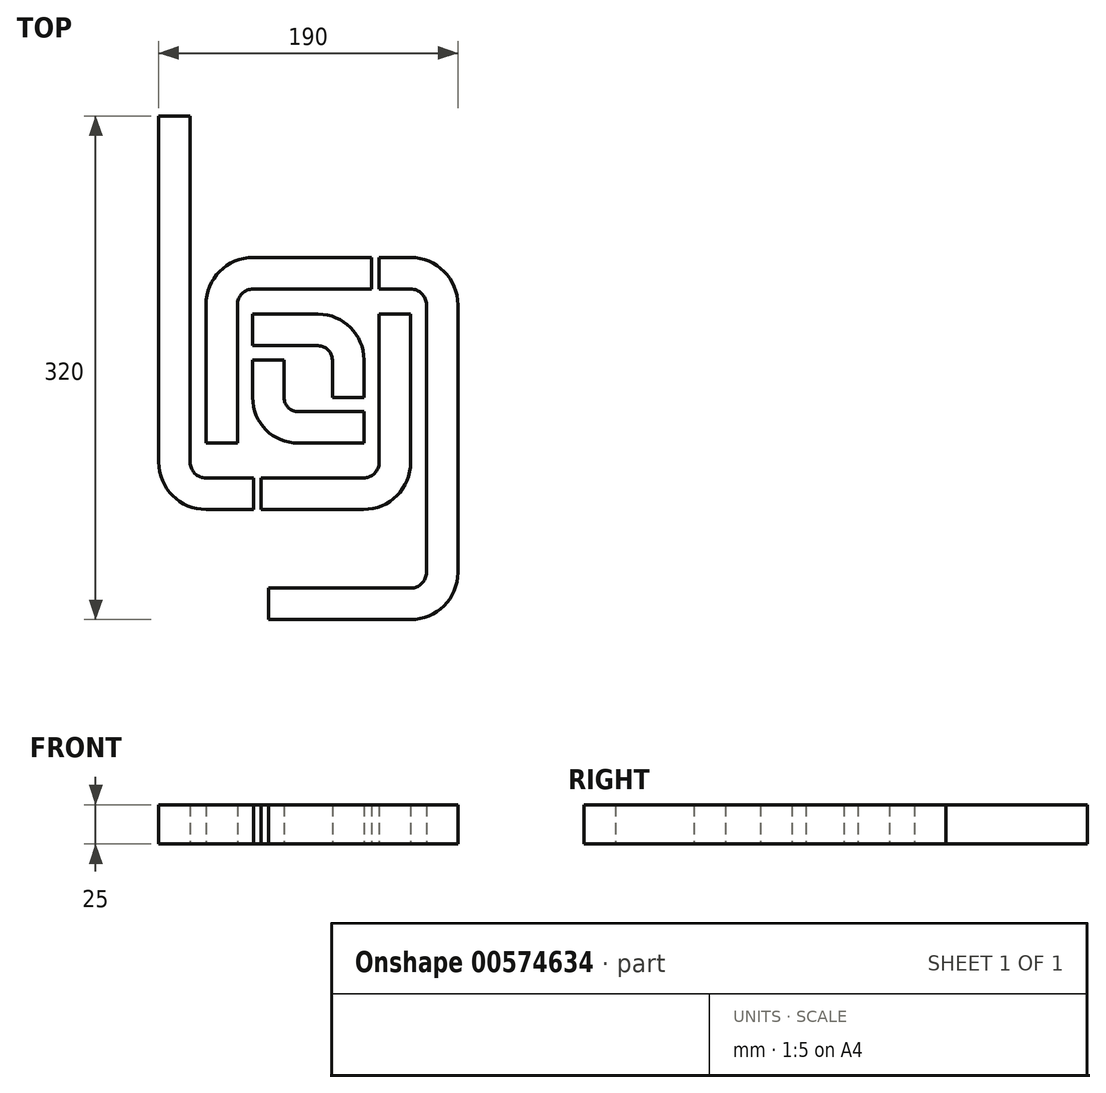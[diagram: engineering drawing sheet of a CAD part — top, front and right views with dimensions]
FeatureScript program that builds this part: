
annotation { "Feature Type Name" : "Feature", "Feature Type Description" : "" }
export const myFeature = defineFeature(function(context is Context, id is Id, definition is map)
    precondition{}
    {
        {
            var Q0;
            Q0=qCreatedBy(makeId("Top.planeOp"),FACE);
            var sketch = newSketch(context, id + "F0", { "sketchPlane" : qUnion([Q0])});
            skPoint(sketch, "E0.startSnap0", {"position": v(38.95, 26.54) * mm});
            skArc(sketch, "E1", {"start": v(-203.39, -102.03) * mm, "mid": v(-200.46, -109.1) * mm, "end": v(-193.39, -112.03) * mm});
            skArc(sketch, "E2", {"start": v(-163.39, 7.97) * mm, "mid": v(-170.46, 5.04) * mm, "end": v(-173.39, -2.03) * mm});
            skArc(sketch, "E3", {"start": v(-143.72, -60.98) * mm, "mid": v(-141.1, -67.3) * mm, "end": v(-134.77, -69.93) * mm});
            skArc(sketch, "E4", {"start": v(-93.39, -112.03) * mm, "mid": v(-86.32, -109.1) * mm, "end": v(-83.39, -102.03) * mm});
            skArc(sketch, "E5", {"start": v(-53.39, -2.03) * mm, "mid": v(-56.32, 5.04) * mm, "end": v(-63.39, 7.97) * mm});
            skLineSegment(sketch, "E6", {"start": v(-53.39, -2.03) * mm, "end": v(-53.39, -172.03) * mm});
            skArc(sketch, "E7", {"start": v(-63.39, -182.03) * mm, "mid": v(-56.32, -179.1) * mm, "end": v(-53.39, -172.03) * mm});
            skLineSegment(sketch, "E8", {"start": v(-113.1, -60.98) * mm, "end": v(-113.1, -36.98) * mm});
            skArc(sketch, "E9", {"start": v(-113.1, -36.98) * mm, "mid": v(-115.73, -30.65) * mm, "end": v(-122.05, -28.03) * mm});
            skLineSegment(sketch, "E10", {"start": v(-93.1, -36.98) * mm, "end": v(-93.1, -60.98) * mm});
            skArc(sketch, "E11", {"start": v(-93.1, -36.98) * mm, "mid": v(-101.58, -16.5) * mm, "end": v(-122.05, -8.03) * mm});
            skLineSegment(sketch, "E12", {"start": v(-163.72, -60.98) * mm, "end": v(-163.72, -36.98) * mm});
            skArc(sketch, "E13", {"start": v(-163.72, -60.98) * mm, "mid": v(-155.24, -81.45) * mm, "end": v(-134.77, -89.93) * mm});
            skArc(sketch, "E14", {"start": v(-163.39, 27.97) * mm, "mid": v(-184.6, 19.18) * mm, "end": v(-193.39, -2.03) * mm});
            skArc(sketch, "E15", {"start": v(-33.39, -2.03) * mm, "mid": v(-42.17, 19.18) * mm, "end": v(-63.39, 27.97) * mm});
            skArc(sketch, "E16", {"start": v(-93.39, -132.03) * mm, "mid": v(-72.17, -123.24) * mm, "end": v(-63.39, -102.03) * mm});
            skLineSegment(sketch, "E17", {"start": v(-33.39, -172.03) * mm, "end": v(-33.39, -2.03) * mm});
            skArc(sketch, "E18", {"start": v(-63.39, -202.03) * mm, "mid": v(-42.17, -193.24) * mm, "end": v(-33.39, -172.03) * mm});
            skArc(sketch, "E19", {"start": v(-223.39, -102.03) * mm, "mid": v(-214.6, -123.24) * mm, "end": v(-193.39, -132.03) * mm});
            skLineSegment(sketch, "E20", {"start": v(-203.39, -102.03) * mm, "end": v(-203.39, 117.97) * mm});
            skLineSegment(sketch, "E21", {"start": v(-193.39, -89.93) * mm, "end": v(-193.39, -2.03) * mm});
            skLineSegment(sketch, "E22", {"start": v(-173.39, -89.93) * mm, "end": v(-173.39, -2.03) * mm});
            skLineSegment(sketch, "E23", {"start": v(-173.39, -89.93) * mm, "end": v(-193.39, -89.93) * mm});
            skLineSegment(sketch, "E24", {"start": v(-122.05, -28.03) * mm, "end": v(-163.72, -28.03) * mm});
            skLineSegment(sketch, "E25", {"start": v(-163.72, -28.03) * mm, "end": v(-163.72, -8.03) * mm});
            skLineSegment(sketch, "E26", {"start": v(-163.72, -8.03) * mm, "end": v(-122.05, -8.03) * mm});
            skLineSegment(sketch, "E27", {"start": v(-93.1, -89.93) * mm, "end": v(-134.77, -89.93) * mm});
            skLineSegment(sketch, "E28", {"start": v(-93.1, -69.93) * mm, "end": v(-93.1, -89.93) * mm});
            skLineSegment(sketch, "E29", {"start": v(-134.77, -69.93) * mm, "end": v(-93.1, -69.93) * mm});
            skLineSegment(sketch, "E30", {"start": v(-83.39, -8.03) * mm, "end": v(-83.39, -102.03) * mm});
            skLineSegment(sketch, "E31", {"start": v(-63.39, -8.03) * mm, "end": v(-83.39, -8.03) * mm});
            skLineSegment(sketch, "E32", {"start": v(-63.39, -8.03) * mm, "end": v(-63.39, -102.03) * mm});
            skLineSegment(sketch, "E33", {"start": v(-63.39, -182.03) * mm, "end": v(-153.72, -182.03) * mm});
            skLineSegment(sketch, "E34", {"start": v(-153.72, -182.03) * mm, "end": v(-153.72, -202.03) * mm});
            skLineSegment(sketch, "E35", {"start": v(-153.72, -202.03) * mm, "end": v(-63.39, -202.03) * mm});
            skLineSegment(sketch, "E36", {"start": v(-113.1, -60.98) * mm, "end": v(-93.1, -60.98) * mm});
            skLineSegment(sketch, "E37", {"start": v(-163.72, -36.98) * mm, "end": v(-143.72, -36.98) * mm});
            skLineSegment(sketch, "E38", {"start": v(-223.39, -102.03) * mm, "end": v(-223.39, 117.97) * mm});
            skLineSegment(sketch, "E39", {"start": v(-223.39, 117.97) * mm, "end": v(-203.39, 117.97) * mm});
            skLineSegment(sketch, "E40", {"start": v(-213.39, 74.6) * mm, "end": v(-213.39, -102.03) * mm, "construction": true});
            skLineSegment(sketch, "E41", {"start": v(-183.39, -89.93) * mm, "end": v(-183.39, -2.58) * mm, "construction": true});
            skLineSegment(sketch, "E42", {"start": v(-73.39, 1.4) * mm, "end": v(-73.39, -102.03) * mm, "construction": true});
            skLineSegment(sketch, "E43", {"start": v(2.28, -79.93) * mm, "end": v(-134.77, -79.93) * mm, "construction": true});
            skLineSegment(sketch, "E44", {"start": v(-103.05, -60.98) * mm, "end": v(-103.05, -36.98) * mm, "construction": true});
            skLineSegment(sketch, "E45", {"start": v(-153.72, -192.03) * mm, "end": v(-2.71, -192.03) * mm, "construction": true});
            skLineSegment(sketch, "E46", {"start": v(-163.39, 17.97) * mm, "end": v(-63.39, 17.97) * mm, "construction": true});
            skLineSegment(sketch, "E47", {"start": v(-153.72, -0.14) * mm, "end": v(-153.72, -60.98) * mm, "construction": true});
            skLineSegment(sketch, "E48", {"start": v(-93.39, -122.03) * mm, "end": v(-193.39, -122.03) * mm, "construction": true});
            skLineSegment(sketch, "E49", {"start": v(-43.39, -2.03) * mm, "end": v(-43.39, -172.03) * mm, "construction": true});
            skArc(sketch, "E50.filletArc", {"start": v(-103.05, -36.98) * mm, "mid": v(-109.12, -23.06) * mm, "end": v(-123.45, -18.03) * mm, "construction": true});
            skArc(sketch, "E51.filletArc", {"start": v(-153.72, -60.98) * mm, "mid": v(-148.17, -74.38) * mm, "end": v(-134.77, -79.93) * mm, "construction": true});
            skArc(sketch, "E52.filletArc", {"start": v(-163.39, 17.97) * mm, "mid": v(-177.53, 12.11) * mm, "end": v(-183.39, -2.03) * mm, "construction": true});
            skArc(sketch, "E53.filletArc", {"start": v(-43.39, -2.03) * mm, "mid": v(-49.24, 12.11) * mm, "end": v(-63.39, 17.97) * mm, "construction": true});
            skArc(sketch, "E54.filletArc", {"start": v(-93.39, -122.03) * mm, "mid": v(-79.24, -116.17) * mm, "end": v(-73.39, -102.03) * mm, "construction": true});
            skArc(sketch, "E55.filletArc", {"start": v(-63.39, -192.03) * mm, "mid": v(-49.24, -186.17) * mm, "end": v(-43.39, -172.03) * mm, "construction": true});
            skArc(sketch, "E56.filletArc", {"start": v(-213.39, -102.03) * mm, "mid": v(-207.53, -116.17) * mm, "end": v(-193.39, -122.03) * mm, "construction": true});
            skLineSegment(sketch, "E57", {"start": v(7.86, -52.03) * mm, "end": v(-8.28, -52.03) * mm, "construction": true});
            skLineSegment(sketch, "E58", {"start": v(-128.39, 4.61) * mm, "end": v(-128.39, -10.57) * mm, "construction": true});
            skLineSegment(sketch, "E59", {"start": v(-163.3, -112.03) * mm, "end": v(-163.3, -132.03) * mm});
            skLineSegment(sketch, "E60", {"start": v(-158.3, -112.03) * mm, "end": v(-158.3, -132.03) * mm});
            skLineSegment(sketch, "E61.trimOffspring", {"start": v(-163.3, -112.03) * mm, "end": v(-193.39, -112.03) * mm});
            skLineSegment(sketch, "E62.trimOffspring", {"start": v(-163.3, -132.03) * mm, "end": v(-193.39, -132.03) * mm});
            skLineSegment(sketch, "E63.trimOffspring", {"start": v(-163.39, 7.97) * mm, "end": v(-88.32, 7.97) * mm});
            skLineSegment(sketch, "E64", {"start": v(-143.72, -60.98) * mm, "end": v(-143.72, -36.98) * mm});
            skLineSegment(sketch, "E65", {"start": v(-123.45, -18.03) * mm, "end": v(-312.6, -18.03) * mm, "construction": true});
            skLineSegment(sketch, "E66", {"start": v(-153.72, -30.56) * mm, "end": v(-153.72, 106.53) * mm, "construction": true});
            skLineSegment(sketch, "E67.trimOffspring", {"start": v(-93.39, -132.03) * mm, "end": v(-158.3, -132.03) * mm});
            skLineSegment(sketch, "E68.trimOffspring", {"start": v(-93.39, -112.03) * mm, "end": v(-158.3, -112.03) * mm});
            skLineSegment(sketch, "E69", {"start": v(-163.39, 27.97) * mm, "end": v(-88.32, 27.97) * mm});
            skLineSegment(sketch, "E70", {"start": v(-83.32, 27.97) * mm, "end": v(-63.39, 27.97) * mm});
            skLineSegment(sketch, "E71", {"start": v(-83.32, 27.97) * mm, "end": v(-83.32, 7.97) * mm});
            skLineSegment(sketch, "E72", {"start": v(-88.32, 27.97) * mm, "end": v(-88.32, 7.97) * mm});
            skLineSegment(sketch, "E73.trimOffspring", {"start": v(-83.32, 7.97) * mm, "end": v(-63.39, 7.97) * mm});
            skPoint(sketch, "E74.middle", {"position": v(-113.1, -36.98) * mm});
            skSolve(sketch);
        }
        {
            var Q0;
            Q0 = qSketchRegion(id + "F0", true);
            extrude(context, id + "F1", {"entities" : qUnion([Q0]), "depth" : 25 * mm, "offsetDistance" : 25 * mm});
        }
    });
